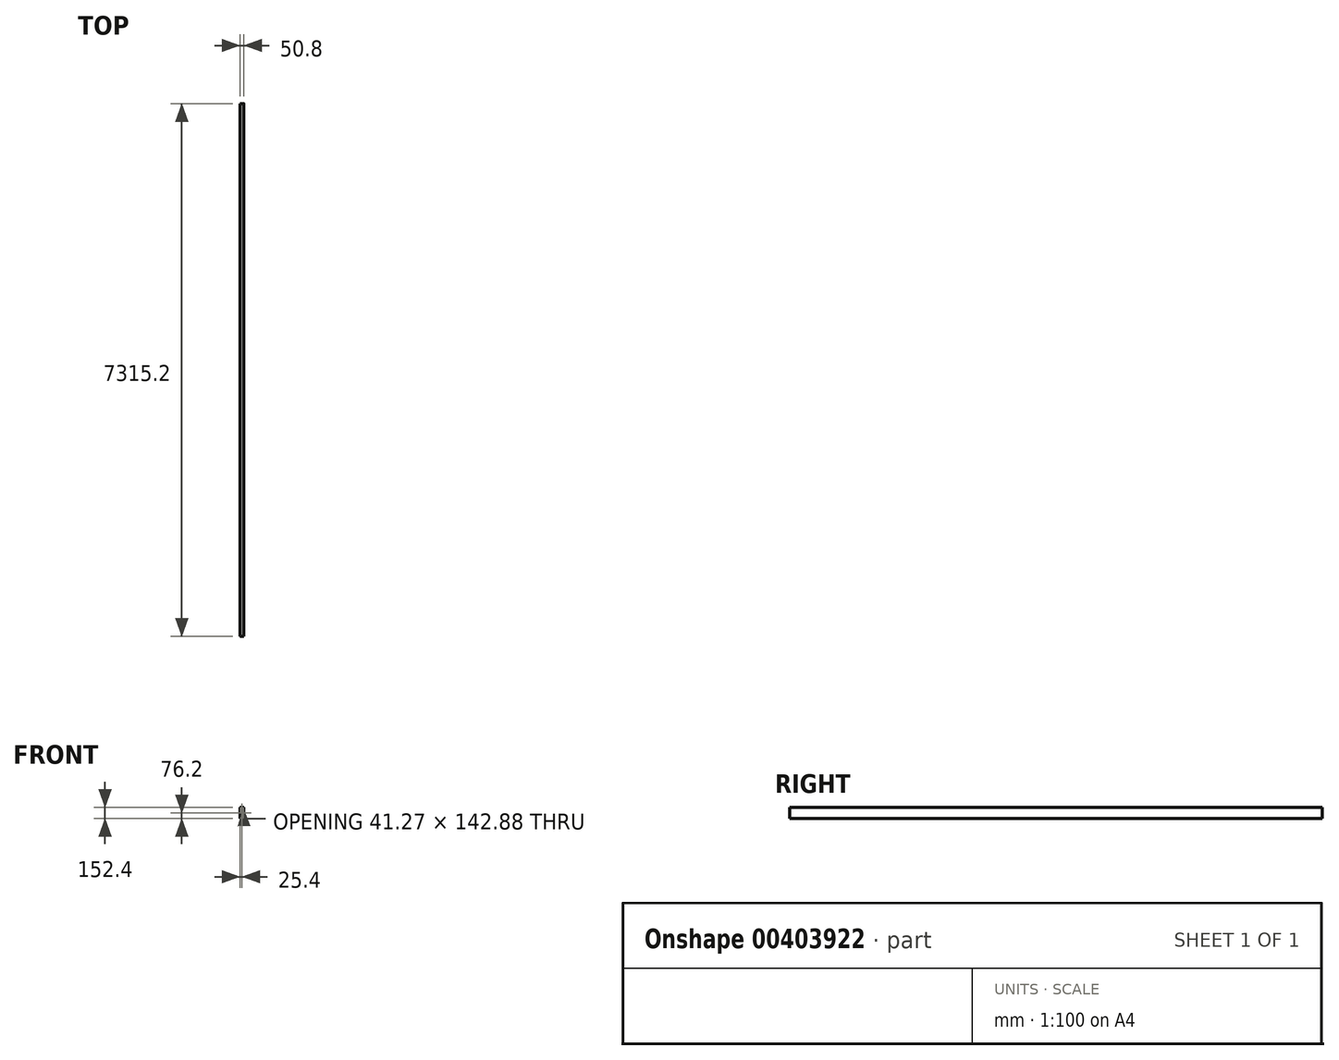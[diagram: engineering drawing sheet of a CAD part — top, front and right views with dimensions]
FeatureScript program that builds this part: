
annotation { "Feature Type Name" : "Feature", "Feature Type Description" : "" }
export const myFeature = defineFeature(function(context is Context, id is Id, definition is map)
    precondition{}
    {
        {
            var Q0;
            Q0=qCreatedBy(makeId("Front.planeOp"),FACE);
            var sketch = newSketch(context, id + "F0", { "sketchPlane" : qUnion([Q0])});
            skLineSegment(sketch, "E0.bottom", {"start": v(19.05, 76.2) * mm, "end": v(-19.05, 76.2) * mm});
            skLineSegment(sketch, "E0.top", {"start": v(19.05, -76.2) * mm, "end": v(-19.05, -76.2) * mm});
            skLineSegment(sketch, "E0.left", {"start": v(25.4, 69.85) * mm, "end": v(25.4, -69.85) * mm});
            skLineSegment(sketch, "E0.right", {"start": v(-25.4, 69.85) * mm, "end": v(-25.4, -69.85) * mm});
            skPoint(sketch, "E0.middle", {"position": v(0, 0) * mm});
            skPoint(sketch, "E1.visualSharp", {"position": v(-25.4, 76.2) * mm});
            skArc(sketch, "E1.filletArc", {"start": v(-19.05, 76.2) * mm, "mid": v(-23.54, 74.34) * mm, "end": v(-25.4, 69.85) * mm});
            skPoint(sketch, "E2.visualSharp", {"position": v(25.4, 76.2) * mm});
            skArc(sketch, "E2.filletArc", {"start": v(25.4, 69.85) * mm, "mid": v(23.54, 74.34) * mm, "end": v(19.05, 76.2) * mm});
            skPoint(sketch, "E3.visualSharp", {"position": v(25.4, -76.2) * mm});
            skArc(sketch, "E3.filletArc", {"start": v(19.05, -76.2) * mm, "mid": v(23.54, -74.34) * mm, "end": v(25.4, -69.85) * mm});
            skPoint(sketch, "E4.visualSharp", {"position": v(-25.4, -76.2) * mm});
            skArc(sketch, "E4.filletArc", {"start": v(-25.4, -69.85) * mm, "mid": v(-23.54, -74.34) * mm, "end": v(-19.05, -76.2) * mm});
            skLineSegment(sketch, "E5.0", {"start": v(15.88, 71.44) * mm, "end": v(-15.87, 71.44) * mm});
            skArc(sketch, "E5.1", {"start": v(20.64, 69.85) * mm, "mid": v(20.17, 70.97) * mm, "end": v(19.05, 71.44) * mm});
            skArc(sketch, "E5.2", {"start": v(-19.05, 71.44) * mm, "mid": v(-20.17, 70.97) * mm, "end": v(-20.64, 69.85) * mm});
            skLineSegment(sketch, "E5.3", {"start": v(20.64, 66.67) * mm, "end": v(20.64, -66.67) * mm});
            skLineSegment(sketch, "E5.4", {"start": v(-20.64, 66.67) * mm, "end": v(-20.64, -66.67) * mm});
            skArc(sketch, "E5.5", {"start": v(-20.64, -69.85) * mm, "mid": v(-20.17, -70.97) * mm, "end": v(-19.05, -71.44) * mm});
            skLineSegment(sketch, "E5.6", {"start": v(15.88, -71.44) * mm, "end": v(-15.87, -71.44) * mm});
            skArc(sketch, "E5.7", {"start": v(19.05, -71.44) * mm, "mid": v(20.17, -70.97) * mm, "end": v(20.64, -69.85) * mm});
            skArc(sketch, "E6.0", {"start": v(19.05, -77.79) * mm, "mid": v(24.66, -75.46) * mm, "end": v(26.99, -69.85) * mm});
            skArc(sketch, "E7.filletArc", {"start": v(-15.87, 71.44) * mm, "mid": v(-19.24, 70.04) * mm, "end": v(-20.64, 66.67) * mm});
            skArc(sketch, "E8.filletArc", {"start": v(20.64, 66.67) * mm, "mid": v(19.24, 70.04) * mm, "end": v(15.88, 71.44) * mm});
            skArc(sketch, "E9.filletArc", {"start": v(15.88, -71.44) * mm, "mid": v(19.24, -70.04) * mm, "end": v(20.64, -66.67) * mm});
            skArc(sketch, "E10.filletArc", {"start": v(-20.64, -66.67) * mm, "mid": v(-19.24, -70.04) * mm, "end": v(-15.87, -71.44) * mm});
            skSolve(sketch);
        }
        {
            var Q0;
            Q0 = qSketchRegion(id + "F0", true);
            extrude(context, id + "F1", {"entities" : qUnion([Q0]), "depth" : 7315.2 * mm});
        }
    });
